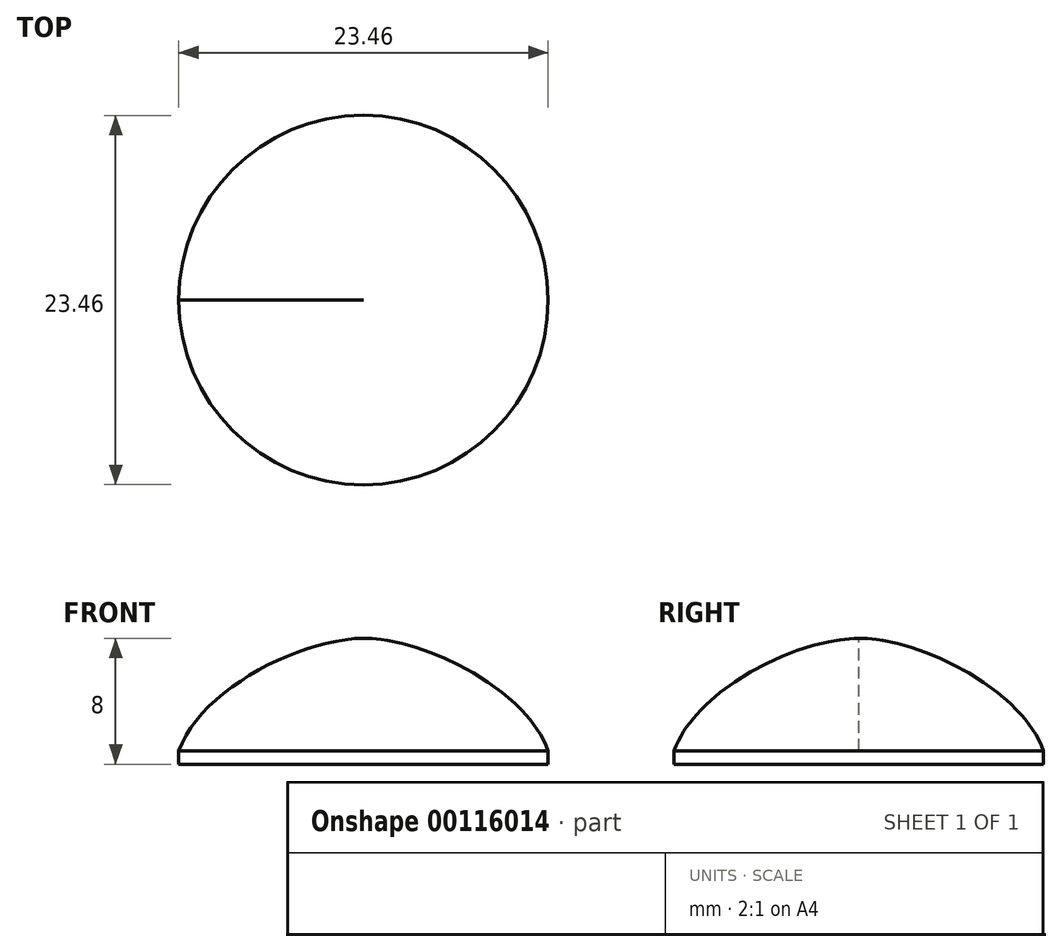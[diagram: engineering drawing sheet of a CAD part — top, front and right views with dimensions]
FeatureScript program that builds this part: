
annotation { "Feature Type Name" : "Feature", "Feature Type Description" : "" }
export const myFeature = defineFeature(function(context is Context, id is Id, definition is map)
    precondition{}
    {
        {
            var Q0;
            Q0=qCreatedBy(makeId("Front.planeOp"),FACE);
            var sketch = newSketch(context, id + "F0", { "sketchPlane" : qUnion([Q0])});
            skLineSegment(sketch, "E0", {"start": v(0, 0) * mm, "end": v(-11.73, 0) * mm});
            skLineSegment(sketch, "E1", {"start": v(-11.73, 0) * mm, "end": v(-11.73, 0.84) * mm});
            skFitSpline(sketch, "E2", {"points": [v(-11.73, 0.84) * mm, v(0, 8) * mm], "startDerivative": vector(4.06, 11.37) * mm, "endDerivative": vector(12.84, 0.31) * mm});
            skLineSegment(sketch, "E3", {"start": v(0, 8) * mm, "end": v(0, 0) * mm});
            skSolve(sketch);
        }
        {
            var Q0;
            Q0=makeQuery(id+"F0.imprint","IMPRINT",FACE,{"disambiguationData":[TD([[makeQuery(id+"F0.imprint","IMPRINT",EDGE,{"derivedFrom":sQuery(id+"F0.wireOp",EDGE,"E0")}),-1.0]])]});
            var Q1;
            Q1=sQuery(id+"F0.wireOp",EDGE,"E1");
            var Q2;
            Q2=sQuery(id+"F0.wireOp",EDGE,"E3");
            revolve(context, id + "F1", {"entities" : qUnion([Q0]), "surfaceEntities" : qUnion([Q1]), "axis" : qUnion([Q2]), "revolveType" : RevolveType.FULL});
        }
    });
